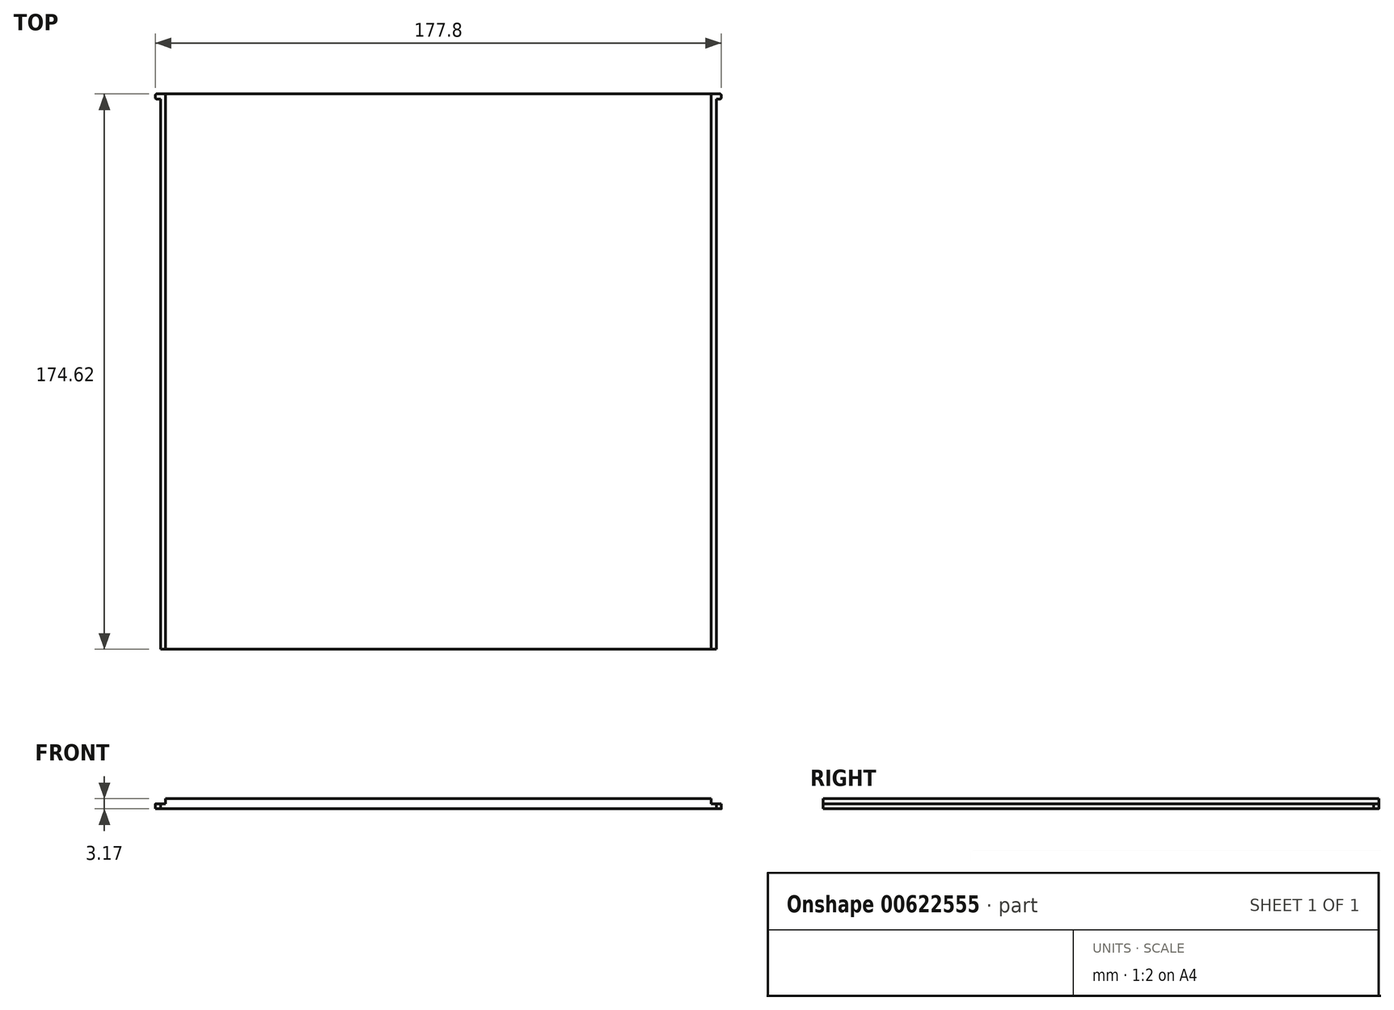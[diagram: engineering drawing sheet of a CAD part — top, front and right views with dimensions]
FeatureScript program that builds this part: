
annotation { "Feature Type Name" : "Feature", "Feature Type Description" : "" }
export const myFeature = defineFeature(function(context is Context, id is Id, definition is map)
    precondition{}
    {
        {
            var Q0;
            Q0=qCreatedBy(makeId("Top.planeOp"),FACE);
            var sketch = newSketch(context, id + "F0", { "sketchPlane" : qUnion([Q0])});
            skLineSegment(sketch, "E0.bottom", {"start": v(-87.31, 88.9) * mm, "end": v(87.31, 88.9) * mm});
            skLineSegment(sketch, "E0.top", {"start": v(-87.31, -85.73) * mm, "end": v(87.31, -85.73) * mm});
            skLineSegment(sketch, "E0.left", {"start": v(-87.31, 87.31) * mm, "end": v(-87.31, -85.73) * mm});
            skLineSegment(sketch, "E0.right", {"start": v(87.31, 87.31) * mm, "end": v(87.31, -85.73) * mm});
            skLineSegment(sketch, "E1.bottom", {"start": v(-87.31, 88.9) * mm, "end": v(-88.52, 88.9) * mm});
            skLineSegment(sketch, "E1.top", {"start": v(-87.31, 87.31) * mm, "end": v(-88.52, 87.31) * mm});
            skLineSegment(sketch, "E1.right", {"start": v(-88.9, 88.52) * mm, "end": v(-88.9, 87.7) * mm});
            skLineSegment(sketch, "E2.bottom", {"start": v(87.31, 88.9) * mm, "end": v(88.52, 88.9) * mm});
            skLineSegment(sketch, "E2.top", {"start": v(87.31, 87.31) * mm, "end": v(88.52, 87.31) * mm});
            skLineSegment(sketch, "E2.right", {"start": v(88.9, 88.52) * mm, "end": v(88.9, 87.7) * mm});
            skPoint(sketch, "E3.visualSharp", {"position": v(-88.9, 87.31) * mm});
            skArc(sketch, "E3.filletArc", {"start": v(-88.9, 87.7) * mm, "mid": v(-88.79, 87.42) * mm, "end": v(-88.52, 87.31) * mm});
            skPoint(sketch, "E4.visualSharp", {"position": v(-88.9, 88.9) * mm});
            skArc(sketch, "E4.filletArc", {"start": v(-88.52, 88.9) * mm, "mid": v(-88.79, 88.79) * mm, "end": v(-88.9, 88.52) * mm});
            skPoint(sketch, "E5.visualSharp", {"position": v(88.9, 88.9) * mm});
            skArc(sketch, "E5.filletArc", {"start": v(88.9, 88.52) * mm, "mid": v(88.79, 88.79) * mm, "end": v(88.52, 88.9) * mm});
            skPoint(sketch, "E6.visualSharp", {"position": v(88.9, 87.31) * mm});
            skArc(sketch, "E6.filletArc", {"start": v(88.52, 87.31) * mm, "mid": v(88.79, 87.42) * mm, "end": v(88.9, 87.7) * mm});
            skSolve(sketch);
        }
        {
            var Q0;
            Q0=qSketchRegion(id+"F0",true);
            extrude(context, id + "F1", {"entities" : qUnion([Q0]), "depth" : 1.59 * mm, "offsetDistance" : 25.4 * mm});
        }
        {
            var Q0;
            Q0=makeQuery(id+"F1.opExtrude","CAP_FACE",FACE,{"disambiguationData":[OSD([sQuery(id+"F0.wireOp",EDGE,"E0.bottom"),sQuery(id+"F0.wireOp",EDGE,"E0.top"),sQuery(id+"F0.wireOp",EDGE,"E0.left"),sQuery(id+"F0.wireOp",EDGE,"E0.right"),sQuery(id+"F0.wireOp",EDGE,"E1.bottom"),sQuery(id+"F0.wireOp",EDGE,"E1.top"),sQuery(id+"F0.wireOp",EDGE,"E1.right"),sQuery(id+"F0.wireOp",EDGE,"E2.bottom"),sQuery(id+"F0.wireOp",EDGE,"E2.top"),sQuery(id+"F0.wireOp",EDGE,"E2.right"),sQuery(id+"F0.wireOp",EDGE,"E3.filletArc"),sQuery(id+"F0.wireOp",EDGE,"E4.filletArc"),sQuery(id+"F0.wireOp",EDGE,"E5.filletArc"),sQuery(id+"F0.wireOp",EDGE,"E6.filletArc")])],"isStart":false});
            var sketch = newSketch(context, id + "F2", { "sketchPlane" : qUnion([Q0])});
            skLineSegment(sketch, "E7.bottom", {"start": v(85.73, -85.73) * mm, "end": v(-85.72, -85.73) * mm});
            skLineSegment(sketch, "E7.top", {"start": v(85.72, 88.9) * mm, "end": v(-85.73, 88.9) * mm});
            skLineSegment(sketch, "E7.left", {"start": v(85.73, -85.73) * mm, "end": v(85.72, 88.9) * mm});
            skLineSegment(sketch, "E7.right", {"start": v(-85.72, -85.73) * mm, "end": v(-85.73, 88.9) * mm});
            skSolve(sketch);
        }
        {
            var Q0;
            Q0=qSketchRegion(id+"F2",true);
            extrude(context, id + "F3", {"entities" : qUnion([Q0]), "operationType" : NewBodyOperationType.ADD, "depth" : 1.59 * mm, "offsetDistance" : 25.4 * mm});
        }
    });
